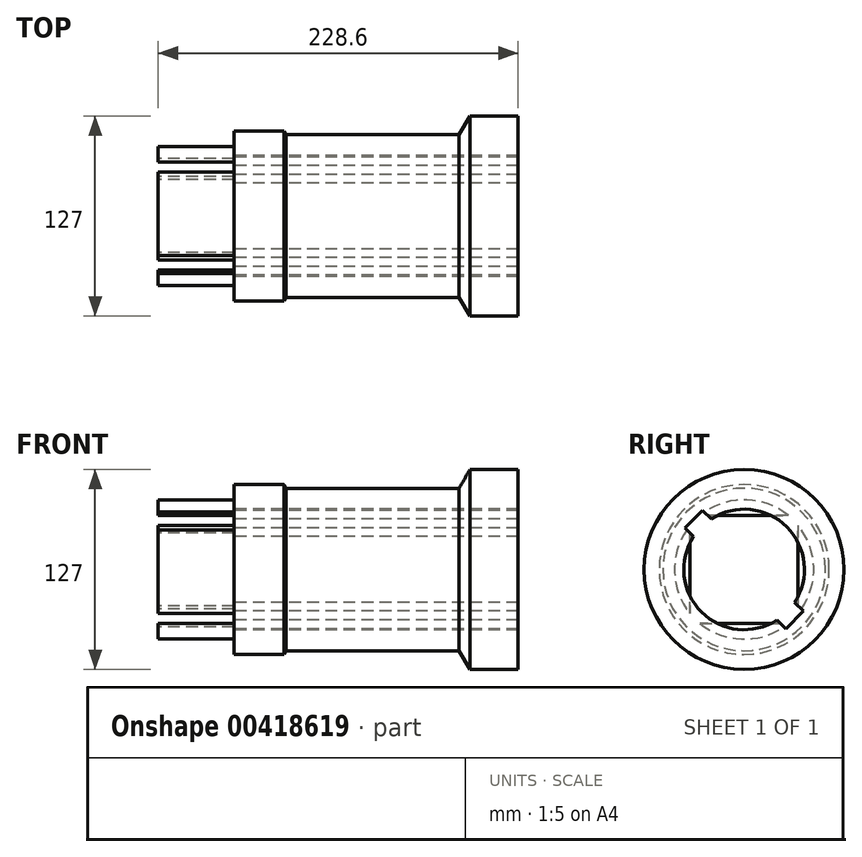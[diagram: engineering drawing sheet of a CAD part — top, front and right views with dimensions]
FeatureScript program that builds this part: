
annotation { "Feature Type Name" : "Feature", "Feature Type Description" : "" }
export const myFeature = defineFeature(function(context is Context, id is Id, definition is map)
    precondition{}
    {
        {
            var Q0;
            Q0=qCreatedBy(makeId("Front.planeOp"),FACE);
            var sketch = newSketch(context, id + "F0", { "sketchPlane" : qUnion([Q0])});
            skLineSegment(sketch, "E0", {"start": v(0, 0) * mm, "end": v(228.6, 0) * mm});
            skLineSegment(sketch, "E1", {"start": v(228.6, 63.5) * mm, "end": v(228.6, 38.3) * mm});
            skLineSegment(sketch, "E2", {"start": v(197.96, 63.5) * mm, "end": v(228.6, 63.5) * mm});
            skLineSegment(sketch, "E3", {"start": v(81.24, 51.6) * mm, "end": v(191.1, 51.6) * mm});
            skLineSegment(sketch, "E4", {"start": v(197.96, 63.5) * mm, "end": v(191.1, 51.6) * mm});
            skLineSegment(sketch, "E5", {"start": v(48.12, 53.98) * mm, "end": v(79.87, 53.98) * mm});
            skLineSegment(sketch, "E6", {"start": v(81.24, 51.6) * mm, "end": v(79.87, 53.98) * mm});
            skLineSegment(sketch, "E7", {"start": v(48.12, 34.3) * mm, "end": v(48.12, 53.98) * mm});
            skLineSegment(sketch, "E8", {"start": v(48.12, 38.3) * mm, "end": v(228.6, 38.3) * mm});
            skLineSegment(sketch, "E9", {"start": v(0, 34.3) * mm, "end": v(48.12, 34.3) * mm});
            skLineSegment(sketch, "E10", {"start": v(0, 34.3) * mm, "end": v(0, 44.26) * mm});
            skLineSegment(sketch, "E11", {"start": v(48.12, 44.26) * mm, "end": v(0, 44.26) * mm});
            skSolve(sketch);
        }
        {
            var Q0;
            Q0 = qSketchRegion(id + "F0", true);
            var Q1;
            Q1=sQuery(id+"F0.wireOp",EDGE,"E0");
            revolve(context, id + "F1", {"entities" : qUnion([Q0]), "axis" : qUnion([Q1]), "revolveType" : RevolveType.FULL});
        }
        {
            var Q0;
            Q0=makeQuery(id+"F1.opRevolve","SWEPT_FACE",FACE,{"disambiguationData":[OSD([sQuery(id+"F0.wireOp",EDGE,"E10")])]});
            cPlane(context, id + "F2", {"entities" : qUnion([Q0]), "cplaneType" : CPlaneType.OFFSET, "offset" : 0 * mm, "width" : 152.4 * mm, "height" : 152.4 * mm});
        }
        {
            var Q0;
            Q0=qCreatedBy(id+"F2.planeOp",FACE);
            var sketch = newSketch(context, id + "F3", { "sketchPlane" : qUnion([Q0])});
            skLineSegment(sketch, "E12", {"start": v(0, 0) * mm, "end": v(0, 169.65) * mm, "construction": true});
            skLineSegment(sketch, "E13", {"start": v(0, 0) * mm, "end": v(180.83, 0) * mm, "construction": true});
            skLineSegment(sketch, "E14.bottom", {"start": v(-34.3, 34.3) * mm, "end": v(34.3, 34.3) * mm});
            skLineSegment(sketch, "E14.top", {"start": v(-34.3, -34.3) * mm, "end": v(34.3, -34.3) * mm});
            skLineSegment(sketch, "E14.left", {"start": v(-34.3, 34.3) * mm, "end": v(-34.3, -34.3) * mm});
            skLineSegment(sketch, "E14.right", {"start": v(34.3, 34.3) * mm, "end": v(34.29, -34.3) * mm});
            skSolve(sketch);
        }
        {
            var Q0;
            Q0 = qSketchRegion(id + "F3", true);
            var Q1;
            {var subQ0=sQuery(id+"F0.wireOp",EDGE,"E7");Q1=makeQuery(id+"F1.opRevolve","SWEPT_FACE",FACE,{"disambiguationData":[OSD([subQ0]),TDD([makeQuery(id+"F0.imprint","IMPRINT",EDGE,{"disambiguationData":[TD([[makeQuery(id+"F0.imprint","INTERSECT",VERTEX,{"derivedFrom":[sQuery(id+"F0.wireOp",EDGE,"E5"),subQ0]}),1.0]])],"derivedFrom":subQ0})])]});}
            extrude(context, id + "F4", {"entities" : qUnion([Q0]), "operationType" : NewBodyOperationType.REMOVE, "endBound" : BoundingType.UP_TO_SURFACE, "oppositeDirection" : true, "endBoundEntityFace" : qUnion([Q1]), "depth" : 25.4 * mm});
        }
        {
            var Q0;
            {var subQ0=sQuery(id+"F0.wireOp",EDGE,"E7");Q0=makeQuery(id+"F4.boolean.opBoolean","MERGE",FACE,{"derivedFrom":[makeQuery(id+"F1.opRevolve","SWEPT_FACE",FACE,{"disambiguationData":[OSD([subQ0]),TDD([makeQuery(id+"F0.imprint","IMPRINT",EDGE,{"disambiguationData":[TD([[makeQuery(id+"F0.imprint","INTERSECT",VERTEX,{"derivedFrom":[sQuery(id+"F0.wireOp",EDGE,"E5"),subQ0]}),1.0]])],"derivedFrom":subQ0})])]}),makeQuery(id+"F4.opExtrude","CAP_FACE",FACE,{"disambiguationData":[OSD([sQuery(id+"F3.wireOp",EDGE,"E14.bottom"),sQuery(id+"F3.wireOp",EDGE,"E14.top"),sQuery(id+"F3.wireOp",EDGE,"E14.left"),sQuery(id+"F3.wireOp",EDGE,"E14.right")])],"isStart":false})]});}
            cPlane(context, id + "F5", {"entities" : qUnion([Q0]), "cplaneType" : CPlaneType.OFFSET, "offset" : 0 * mm, "width" : 152.4 * mm, "height" : 152.4 * mm});
        }
        {
            var Q0;
            Q0=qCreatedBy(id+"F5.planeOp",FACE);
            var sketch = newSketch(context, id + "F6", { "sketchPlane" : qUnion([Q0])});
            skLineSegment(sketch, "E15", {"start": v(0, 0) * mm, "end": v(88.77, 0) * mm, "construction": true});
            skLineSegment(sketch, "E16", {"start": v(0, 0) * mm, "end": v(72.74, 72.74) * mm, "construction": true});
            skLineSegment(sketch, "E17", {"start": v(0, 0) * mm, "end": v(72.74, 72.74) * mm});
            skLineSegment(sketch, "E18.0", {"start": v(5.6, -5.6) * mm, "end": v(37.6, 26.39) * mm});
            skLineSegment(sketch, "E19.MirrorCS", {"start": v(-5.6, 5.6) * mm, "end": v(26.39, 37.6) * mm});
            skLineSegment(sketch, "E20", {"start": v(-5.6, 5.6) * mm, "end": v(5.6, -5.6) * mm});
            skLineSegment(sketch, "E21.0", {"start": v(26.39, 37.6) * mm, "end": v(37.6, 26.39) * mm});
            skPoint(sketch, "E22.orphan", {"position": v(78.35, 67.13) * mm});
            skPoint(sketch, "E23.orphan", {"position": v(67.13, 78.35) * mm});
            skLineSegment(sketch, "E24.MirrorCS", {"start": v(-5.6, 5.6) * mm, "end": v(-37.6, -26.39) * mm});
            skLineSegment(sketch, "E25.MirrorCS", {"start": v(-37.6, -26.39) * mm, "end": v(-26.39, -37.6) * mm});
            skLineSegment(sketch, "E26.MirrorCS", {"start": v(5.6, -5.6) * mm, "end": v(-26.39, -37.6) * mm});
            skSolve(sketch);
        }
        {
            var Q0;
            Q0 = qSketchRegion(id + "F6", true);
            extrude(context, id + "F7", {"entities" : qUnion([Q0]), "operationType" : NewBodyOperationType.REMOVE, "endBound" : BoundingType.SYMMETRIC, "oppositeDirection" : true, "depth" : 406.4 * mm});
        }
    });
